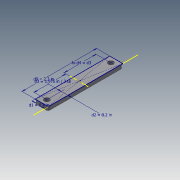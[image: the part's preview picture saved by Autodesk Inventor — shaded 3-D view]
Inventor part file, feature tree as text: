
AUTODESK INVENTOR PART (.ipt)
format: ipt  version: 2020.3 (Build 243373000, 373)  size: 110,592 bytes
history: native  units: in
note: dims shown in document units (in); Inventor stores cm internally (conversion verified against a paired STEP export)
features: fillet x2, sketch x1, extrude x1, hole x1
ambient origin geometry x8: Origin, YZ Plane, XZ Plane, XY Plane, X Axis, Y Axis, Z Axis, Center Point
bodies: Solid1 (feature_tree)
feature tree (5):
  sketch  "Sketch1"  dims[d0=2.3in d1=0.4in d2=0.2in d3=0.9875in d4=0.9875in d5=0.125in d6=0.0in d7=0.05in d8=0.05in d9=0.16in d10=0.75in d11=0.375in d12=0.25in d13=0.5635in d14=1.0in d15=0.8108in]
  extrude  "Extrusion1"  Depth=0.4in
  fillet  "Fillet1"  Radius=0.2in
  fillet  "Fillet2"  Radius=0.9875in
  hole  "Hole1"  [1 undecoded]
note: 1 required parameter value undecoded (feature->parameter linkage not recoverable at this tier; creation-order binding heuristic only, values carry confidence <= 0.55)
